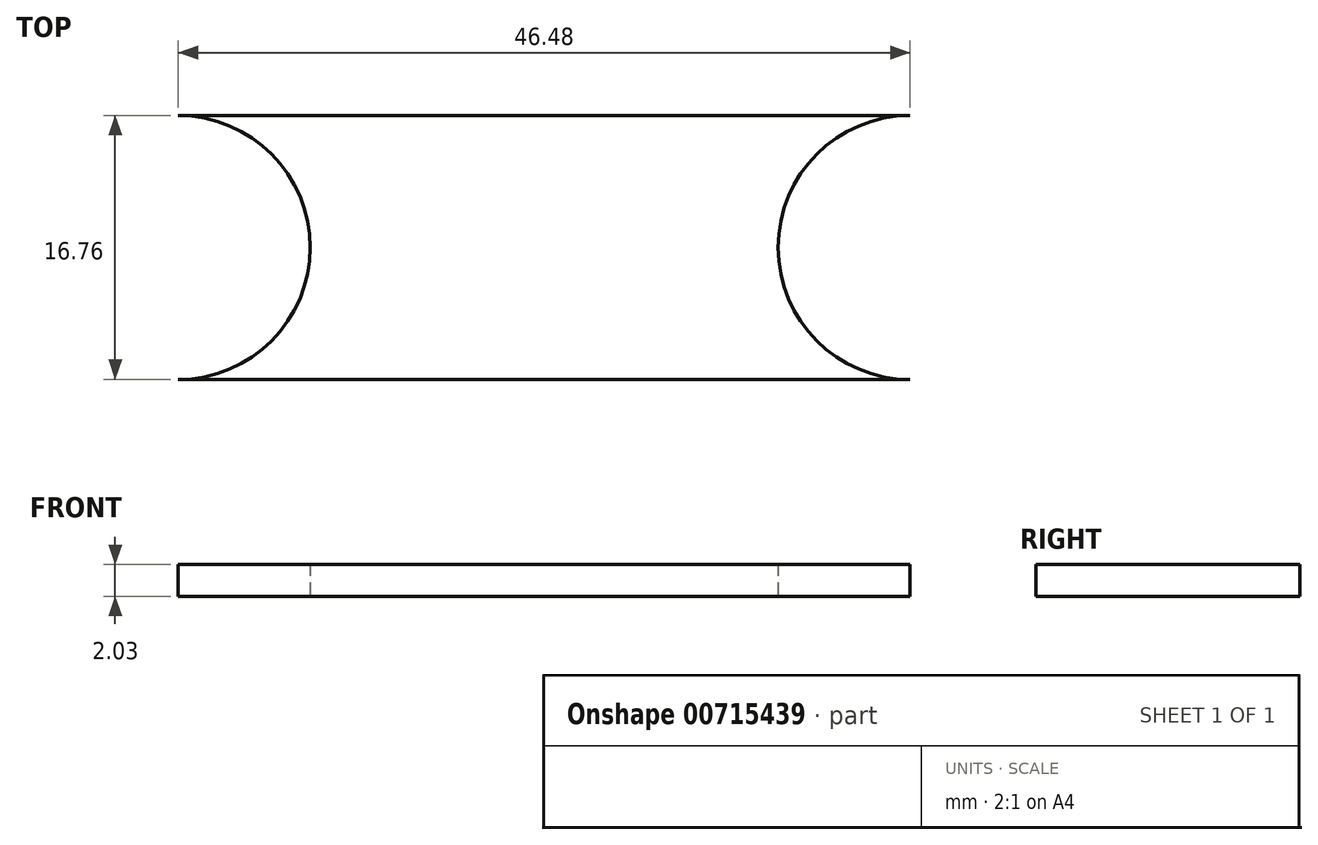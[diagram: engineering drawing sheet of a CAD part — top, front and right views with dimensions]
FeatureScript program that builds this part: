
annotation { "Feature Type Name" : "Feature", "Feature Type Description" : "" }
export const myFeature = defineFeature(function(context is Context, id is Id, definition is map)
    precondition{}
    {
        {
            var Q0;
            Q0=qCreatedBy(makeId("Top.planeOp"),FACE);
            var sketch = newSketch(context, id + "F0", { "sketchPlane" : qUnion([Q0])});
            skLineSegment(sketch, "E0.bottom", {"start": v(23.24, 8.38) * mm, "end": v(-23.24, 8.38) * mm});
            skLineSegment(sketch, "E0.top", {"start": v(23.24, -8.38) * mm, "end": v(-23.24, -8.38) * mm});
            skPoint(sketch, "E0.middle", {"position": v(0, 0) * mm});
            skArc(sketch, "E1", {"start": v(-23.24, -8.38) * mm, "mid": v(-14.86, 0) * mm, "end": v(-23.24, 8.38) * mm});
            skArc(sketch, "E2", {"start": v(23.24, 8.38) * mm, "mid": v(14.86, 0) * mm, "end": v(23.24, -8.38) * mm});
            skSolve(sketch);
        }
        {
            var Q0;
            Q0=makeQuery(id+"F0.imprint","IMPRINT",FACE,{"disambiguationData":[TD([[makeQuery(id+"F0.imprint","IMPRINT",EDGE,{"derivedFrom":sQuery(id+"F0.wireOp",EDGE,"E0.bottom")}),1.0]])]});
            extrude(context, id + "F1", {"entities" : qUnion([Q0]), "depth" : 2.03 * mm, "offsetDistance" : 25.4 * mm});
        }
    });
